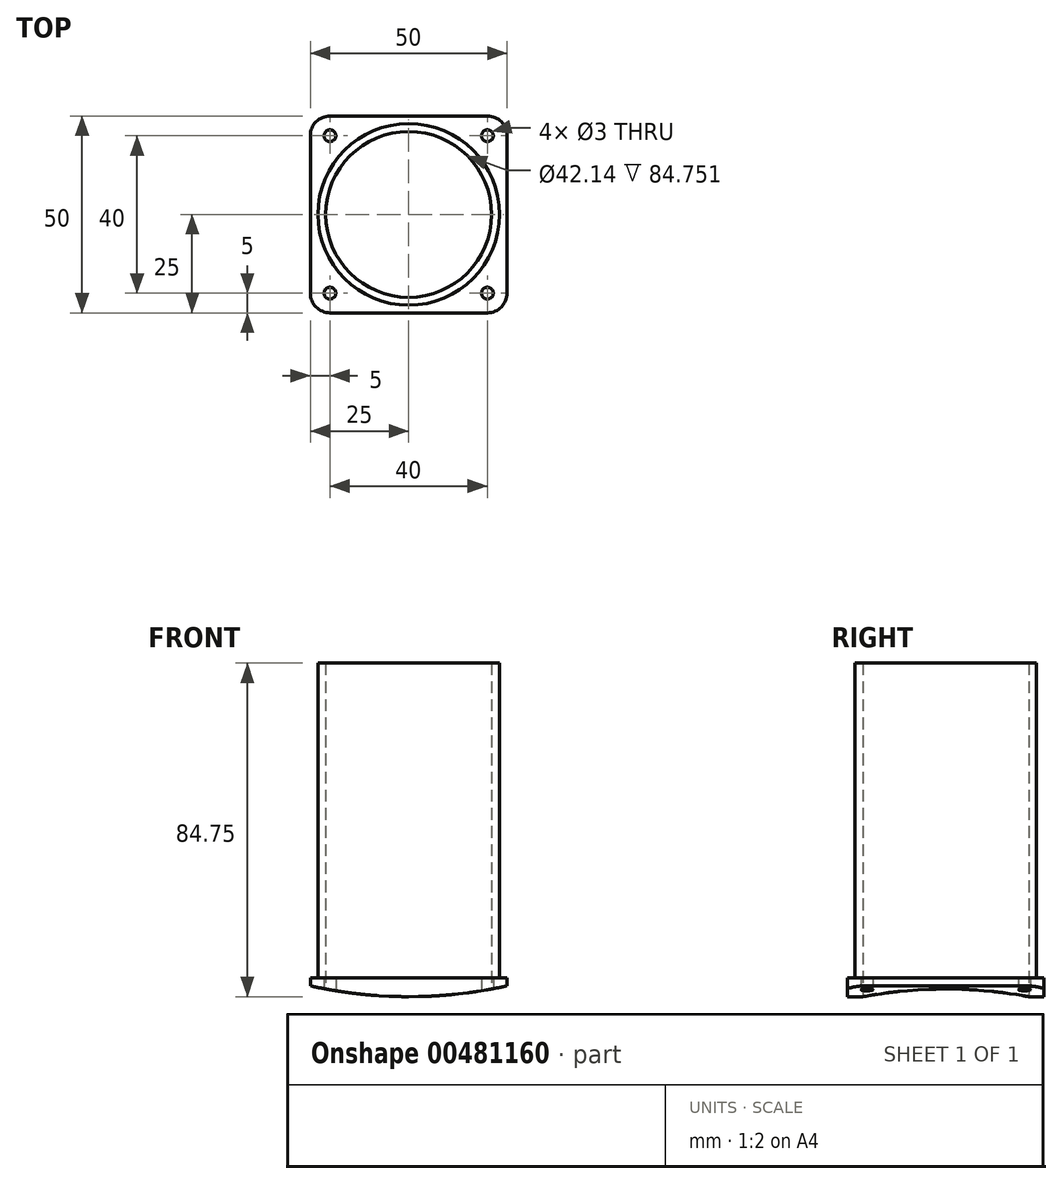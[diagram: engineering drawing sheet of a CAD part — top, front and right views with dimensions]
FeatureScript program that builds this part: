
annotation { "Feature Type Name" : "Feature", "Feature Type Description" : "" }
export const myFeature = defineFeature(function(context is Context, id is Id, definition is map)
    precondition{}
    {
        {
            var Q0;
            Q0=qCreatedBy(makeId("Top.planeOp"),FACE);
            var sketch = newSketch(context, id + "F0", { "sketchPlane" : qUnion([Q0])});
            skLineSegment(sketch, "E0", {"start": v(0, 70.57) * mm, "end": v(0, -91.76) * mm, "construction": true});
            skLineSegment(sketch, "E1", {"start": v(-109.37, 0) * mm, "end": v(112.01, 0) * mm, "construction": true});
            skLineSegment(sketch, "E2.bottom", {"start": v(25, 25) * mm, "end": v(-25, 25) * mm});
            skLineSegment(sketch, "E2.top", {"start": v(25, -25) * mm, "end": v(-25, -25) * mm});
            skLineSegment(sketch, "E2.left", {"start": v(25, 25) * mm, "end": v(25, -25) * mm});
            skLineSegment(sketch, "E2.right", {"start": v(-25, 25) * mm, "end": v(-25, -25) * mm});
            skPoint(sketch, "E2.middle", {"position": v(0, 0) * mm});
            skLineSegment(sketch, "E3.bottom", {"start": v(20, 20) * mm, "end": v(-20, 20) * mm, "construction": true});
            skLineSegment(sketch, "E3.top", {"start": v(20, -20) * mm, "end": v(-20, -20) * mm, "construction": true});
            skLineSegment(sketch, "E3.left", {"start": v(20, 20) * mm, "end": v(20, -20) * mm, "construction": true});
            skLineSegment(sketch, "E3.right", {"start": v(-20, 20) * mm, "end": v(-20, -20) * mm, "construction": true});
            skCircle(sketch, "E4", {"center": v(20, 20) * mm, "radius": 1.5 * mm});
            skCircle(sketch, "E5.MirrorC", {"center": v(-20, 20) * mm, "radius": 1.5 * mm});
            skCircle(sketch, "E6.MirrorC", {"center": v(20, -20) * mm, "radius": 1.5 * mm});
            skCircle(sketch, "E7.MirrorC", {"center": v(-20, -20) * mm, "radius": 1.5 * mm});
            skCircle(sketch, "E8.0", {"center": v(0, 0) * mm, "radius": 21.07 * mm});
            skSolve(sketch);
        }
        {
            var Q0;
            Q0=makeQuery(id+"F0.imprint","IMPRINT",FACE,{"disambiguationData":[TD([[makeQuery(id+"F0.imprint","IMPRINT",EDGE,{"derivedFrom":sQuery(id+"F0.wireOp",EDGE,"E2.bottom")}),1.0]])]});
            extrude(context, id + "F1", {"entities" : qUnion([Q0]), "depth" : 8 * mm, "offsetDistance" : 25 * mm});
        }
        {
            var Q0;
            Q0=makeQuery(id+"F1.opExtrude","SWEPT_FACE",FACE,{"disambiguationData":[OSD([sQuery(id+"F0.wireOp",EDGE,"E2.top")])]});
            var sketch = newSketch(context, id + "F2", { "sketchPlane" : qUnion([Q0])});
            skLineSegment(sketch, "E9", {"start": v(0, 0) * mm, "end": v(0, 132.13) * mm, "construction": true});
            skPoint(sketch, "E9.endSnap0", {"position": v(0, 0) * mm});
            skPoint(sketch, "E10", {"position": v(-25, 6) * mm});
            skPoint(sketch, "E11.MirrorP", {"position": v(25, 6) * mm});
            skCircle(sketch, "E12", {"center": v(0, 118.25) * mm, "radius": 115 * mm});
            skPoint(sketch, "E12.third.point", {"position": v(0, 233.25) * mm});
            skSolve(sketch);
        }
        {
            var Q0;
            {var subQ1=sQuery(id+"F0.wireOp",EDGE,"E2.top");var subQ6=makeQuery(id+"F1.opExtrude","CAP_EDGE",EDGE,{"disambiguationData":[OSD([subQ1])],"isStart":true});Q0=makeQuery(id+"F2.imprint","IMPRINT",FACE,{"disambiguationData":[TD([[makeQuery(id+"F2.imprint","IMPRINT",EDGE,{"derivedFrom":subQ6}),-1.0]])]});}
            extrude(context, id + "F3", {"entities" : qUnion([Q0]), "operationType" : NewBodyOperationType.REMOVE, "oppositeDirection" : true, "depth" : 100 * mm, "offsetDistance" : 25 * mm});
        }
        {
            var Q0;
            Q0=makeQuery(id+"F1.opExtrude","CAP_FACE",FACE,{"disambiguationData":[OSD([sQuery(id+"F0.wireOp",EDGE,"E2.bottom"),sQuery(id+"F0.wireOp",EDGE,"E2.top"),sQuery(id+"F0.wireOp",EDGE,"E2.left"),sQuery(id+"F0.wireOp",EDGE,"E2.right"),sQuery(id+"F0.wireOp",EDGE,"E4"),sQuery(id+"F0.wireOp",EDGE,"E5.MirrorC"),sQuery(id+"F0.wireOp",EDGE,"E6.MirrorC"),sQuery(id+"F0.wireOp",EDGE,"E7.MirrorC"),sQuery(id+"F0.wireOp",EDGE,"E8.0")])],"isStart":false});
            var sketch = newSketch(context, id + "F4", { "sketchPlane" : qUnion([Q0])});
            skCircle(sketch, "E13.0", {"center": v(0, 0) * mm, "radius": 23.07 * mm});
            skSolve(sketch);
        }
        {
            var Q0;
            Q0=makeQuery(id+"F4.imprint","IMPRINT",FACE,{"disambiguationData":[TD([[makeQuery(id+"F4.imprint","IMPRINT",EDGE,{"derivedFrom":sQuery(id+"F4.wireOp",EDGE,"E13.0")}),1.0]])]});
            extrude(context, id + "F5", {"entities" : qUnion([Q0]), "operationType" : NewBodyOperationType.ADD, "depth" : 80 * mm, "offsetDistance" : 25 * mm});
        }
        {
            var Q0;
            Q0=makeQuery(id+"F1.opExtrude","SWEPT_EDGE",EDGE,{"disambiguationData":[OSD([sQuery(id+"F0.wireOp",EDGE,"E2.top"),sQuery(id+"F0.wireOp",EDGE,"E2.left")])]});
            var Q1;
            Q1=makeQuery(id+"F1.opExtrude","SWEPT_EDGE",EDGE,{"disambiguationData":[OSD([sQuery(id+"F0.wireOp",EDGE,"E2.bottom"),sQuery(id+"F0.wireOp",EDGE,"E2.left")])]});
            var Q2;
            Q2=makeQuery(id+"F1.opExtrude","SWEPT_EDGE",EDGE,{"disambiguationData":[OSD([sQuery(id+"F0.wireOp",EDGE,"E2.bottom"),sQuery(id+"F0.wireOp",EDGE,"E2.right")])]});
            var Q3;
            Q3=makeQuery(id+"F1.opExtrude","SWEPT_EDGE",EDGE,{"disambiguationData":[OSD([sQuery(id+"F0.wireOp",EDGE,"E2.top"),sQuery(id+"F0.wireOp",EDGE,"E2.right")])]});
            fillet(context, id + "F6", {"entities" : qUnion([Q0, Q1, Q2, Q3]), "radius" : 5 * mm, "tangentPropagation" : true, "allowEdgeOverflow" : false});
        }
    });
